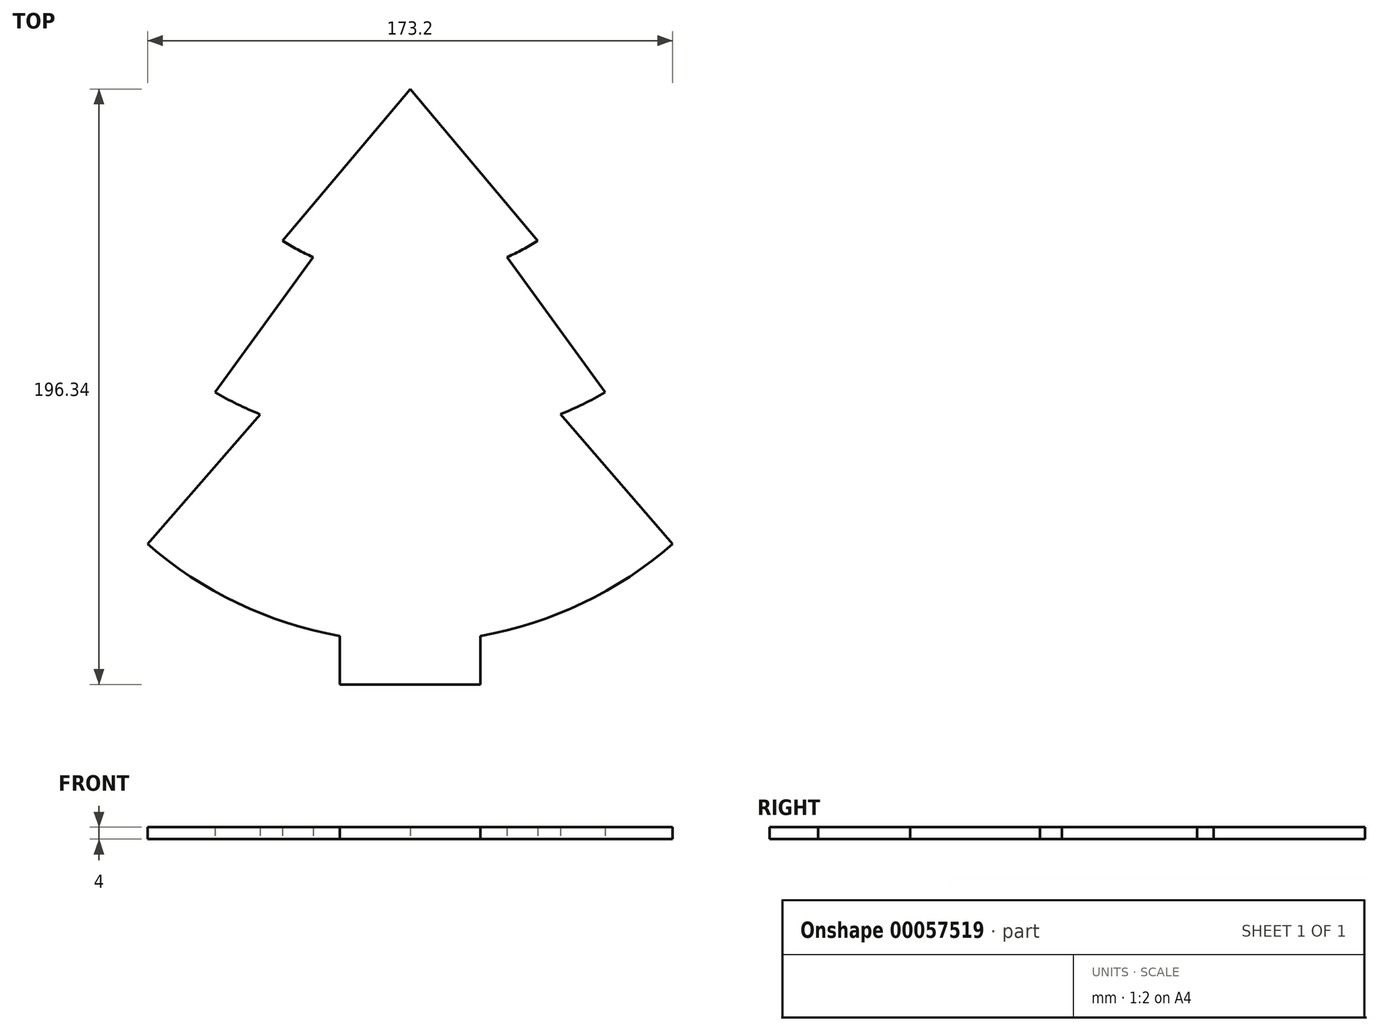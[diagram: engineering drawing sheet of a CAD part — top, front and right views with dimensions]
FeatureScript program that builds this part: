
annotation { "Feature Type Name" : "Feature", "Feature Type Description" : "" }
export const myFeature = defineFeature(function(context is Context, id is Id, definition is map)
    precondition{}
    {
        {
            var Q0;
            Q0=qCreatedBy(makeId("Top.planeOp"),FACE);
            var sketch = newSketch(context, id + "F0", { "sketchPlane" : qUnion([Q0])});
            skCircle(sketch, "E0.cCircle", {"center": v(0, 0) * mm, "radius": 50 * mm, "construction": true});
            skLineSegment(sketch, "E0.0", {"start": v(86.6, -50) * mm, "end": v(-86.6, -50) * mm, "construction": true});
            skLineSegment(sketch, "E0.1", {"start": v(-86.6, -50) * mm, "end": v(0, 100) * mm, "construction": true});
            skLineSegment(sketch, "E0.2", {"start": v(0, 100) * mm, "end": v(86.6, -50) * mm, "construction": true});
            skPoint(sketch, "E0.0.midPoint", {"position": v(0, -50) * mm});
            skLineSegment(sketch, "E1", {"start": v(0, -50) * mm, "end": v(0, 100) * mm, "construction": true});
            skLineSegment(sketch, "E2", {"start": v(-42.16, 50) * mm, "end": v(42.16, 50) * mm, "construction": true});
            skLineSegment(sketch, "E3", {"start": v(-64.38, 0) * mm, "end": v(64.38, 0) * mm, "construction": true});
            skPoint(sketch, "E4", {"position": v(0, 50) * mm});
            skLineSegment(sketch, "E5", {"start": v(-86.6, -50) * mm, "end": v(0, 144.87) * mm, "construction": true});
            skLineSegment(sketch, "E6", {"start": v(0, 144.87) * mm, "end": v(86.6, -50) * mm, "construction": true});
            skArc(sketch, "E7", {"start": v(-42.16, 50) * mm, "mid": v(0, 37.82) * mm, "end": v(42.16, 50) * mm});
            skArc(sketch, "E8", {"start": v(-64.38, 0) * mm, "mid": v(0, -17.07) * mm, "end": v(64.38, 0) * mm});
            skArc(sketch, "E9", {"start": v(-86.6, -50) * mm, "mid": v(0, -82.4) * mm, "end": v(86.6, -50) * mm});
            skLineSegment(sketch, "E10", {"start": v(-64.38, 0) * mm, "end": v(-32, 44.58) * mm});
            skLineSegment(sketch, "E11", {"start": v(64.38, 0) * mm, "end": v(32, 44.58) * mm});
            skLineSegment(sketch, "E12", {"start": v(42.16, 50) * mm, "end": v(0, 100) * mm});
            skLineSegment(sketch, "E13", {"start": v(-42.16, 50) * mm, "end": v(0, 100) * mm});
            skLineSegment(sketch, "E14", {"start": v(-86.6, -50) * mm, "end": v(0, 49.55) * mm});
            skLineSegment(sketch, "E15", {"start": v(0, 50) * mm, "end": v(86.6, -50) * mm});
            skLineSegment(sketch, "E16.bottom", {"start": v(23.17, -50) * mm, "end": v(-23.17, -50) * mm});
            skLineSegment(sketch, "E16.top", {"start": v(23.17, -96.34) * mm, "end": v(-23.17, -96.34) * mm});
            skLineSegment(sketch, "E16.left", {"start": v(23.17, -50) * mm, "end": v(23.17, -96.34) * mm});
            skLineSegment(sketch, "E16.right", {"start": v(-23.17, -50) * mm, "end": v(-23.17, -96.34) * mm});
            skSolve(sketch);
        }
        {
            var Q0;
            Q0 = qSketchRegion(id + "F0", true);
            extrude(context, id + "F1", {"entities" : qUnion([Q0]), "depth" : 4 * mm});
        }
    });
